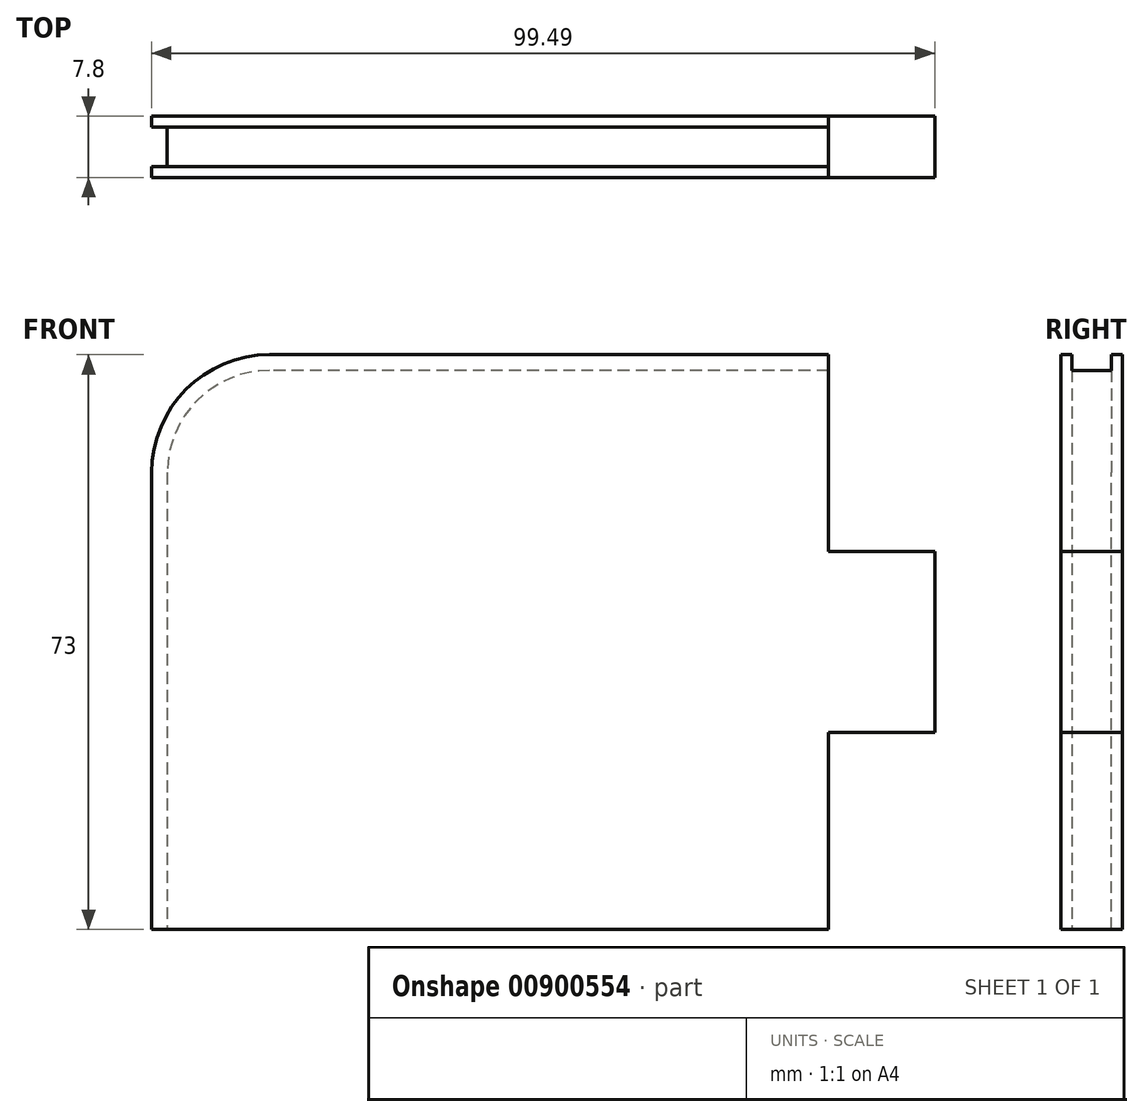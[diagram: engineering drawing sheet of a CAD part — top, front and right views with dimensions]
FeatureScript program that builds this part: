
annotation { "Feature Type Name" : "Feature", "Feature Type Description" : "" }
export const myFeature = defineFeature(function(context is Context, id is Id, definition is map)
    precondition{}
    {
        {
            var Q0;
            Q0=qCreatedBy(makeId("Front.planeOp"),FACE);
            var sketch = newSketch(context, id + "F0", { "sketchPlane" : qUnion([Q0])});
            skLineSegment(sketch, "E0", {"start": v(-28.97, 37.52) * mm, "end": v(42.03, 37.52) * mm});
            skLineSegment(sketch, "E1", {"start": v(42.03, 37.52) * mm, "end": v(42.03, 12.52) * mm});
            skLineSegment(sketch, "E2", {"start": v(42.03, 12.52) * mm, "end": v(55.52, 12.52) * mm});
            skLineSegment(sketch, "E3", {"start": v(55.52, 12.52) * mm, "end": v(55.52, -10.48) * mm});
            skLineSegment(sketch, "E4", {"start": v(55.52, -10.48) * mm, "end": v(42.03, -10.48) * mm});
            skLineSegment(sketch, "E5", {"start": v(42.03, -10.48) * mm, "end": v(42.03, -35.48) * mm});
            skLineSegment(sketch, "E6", {"start": v(42.03, -35.48) * mm, "end": v(-43.97, -35.48) * mm});
            skLineSegment(sketch, "E7", {"start": v(-43.97, -35.48) * mm, "end": v(-43.97, 22.52) * mm});
            skPoint(sketch, "E8.visualSharp", {"position": v(-43.97, 37.52) * mm});
            skArc(sketch, "E8.filletArc", {"start": v(-28.97, 37.52) * mm, "mid": v(-39.58, 33.13) * mm, "end": v(-43.97, 22.52) * mm});
            skSolve(sketch);
        }
        {
            var Q0;
            Q0=makeQuery(id+"F0.imprint","IMPRINT",FACE,{"disambiguationData":[TD([[makeQuery(id+"F0.imprint","IMPRINT",EDGE,{"derivedFrom":sQuery(id+"F0.wireOp",EDGE,"E0")}),-1.0]])]});
            extrude(context, id + "F1", {"entities" : qUnion([Q0]), "oppositeDirection" : true, "depth" : 1.4 * mm, "offsetDistance" : 25 * mm});
        }
        {
            var Q0;
            Q0=makeQuery(id+"F1.opExtrude","CAP_FACE",FACE,{"disambiguationData":[OSD([sQuery(id+"F0.wireOp",EDGE,"E0"),sQuery(id+"F0.wireOp",EDGE,"E1"),sQuery(id+"F0.wireOp",EDGE,"E2"),sQuery(id+"F0.wireOp",EDGE,"E3"),sQuery(id+"F0.wireOp",EDGE,"E4"),sQuery(id+"F0.wireOp",EDGE,"E5"),sQuery(id+"F0.wireOp",EDGE,"E6"),sQuery(id+"F0.wireOp",EDGE,"E7"),sQuery(id+"F0.wireOp",EDGE,"E8.filletArc")])],"isStart":true});
            var sketch = newSketch(context, id + "F2", { "sketchPlane" : qUnion([Q0])});
            skLineSegment(sketch, "E9", {"start": v(42.03, 35.52) * mm, "end": v(-28.97, 35.52) * mm});
            skLineSegment(sketch, "E10", {"start": v(-41.97, 22.52) * mm, "end": v(-41.97, -35.48) * mm});
            skLineSegment(sketch, "E11", {"start": v(-41.97, -35.48) * mm, "end": v(42.03, -35.48) * mm});
            skLineSegment(sketch, "E12", {"start": v(42.03, -35.48) * mm, "end": v(42.03, -10.48) * mm});
            skLineSegment(sketch, "E13", {"start": v(42.03, -10.48) * mm, "end": v(55.52, -10.48) * mm});
            skLineSegment(sketch, "E14", {"start": v(55.52, -10.48) * mm, "end": v(55.52, 12.52) * mm});
            skLineSegment(sketch, "E15", {"start": v(55.52, 12.52) * mm, "end": v(42.03, 12.52) * mm});
            skLineSegment(sketch, "E16", {"start": v(42.03, 12.52) * mm, "end": v(42.03, 35.52) * mm});
            skPoint(sketch, "E17.visualSharp", {"position": v(-41.97, 35.52) * mm});
            skArc(sketch, "E17.filletArc", {"start": v(-28.97, 35.52) * mm, "mid": v(-38.16, 31.72) * mm, "end": v(-41.97, 22.52) * mm});
            skSolve(sketch);
        }
        {
            var Q0;
            Q0 = qSketchRegion(id + "F2", true);
            extrude(context, id + "F3", {"entities" : qUnion([Q0]), "operationType" : NewBodyOperationType.ADD, "depth" : 5 * mm, "offsetDistance" : 25 * mm});
        }
        {
            var Q0;
            Q0=makeQuery(id+"F3.opExtrude","CAP_FACE",FACE,{"disambiguationData":[OSD([sQuery(id+"F2.wireOp",EDGE,"E9"),sQuery(id+"F2.wireOp",EDGE,"E10"),sQuery(id+"F2.wireOp",EDGE,"E11"),sQuery(id+"F2.wireOp",EDGE,"E12"),sQuery(id+"F2.wireOp",EDGE,"E13"),sQuery(id+"F2.wireOp",EDGE,"E14"),sQuery(id+"F2.wireOp",EDGE,"E15"),sQuery(id+"F2.wireOp",EDGE,"E16"),sQuery(id+"F2.wireOp",EDGE,"E17.filletArc")])],"isStart":false});
            var sketch = newSketch(context, id + "F4", { "sketchPlane" : qUnion([Q0])});
            skLineSegment(sketch, "E18", {"start": v(-28.97, 37.52) * mm, "end": v(42.03, 37.52) * mm});
            skLineSegment(sketch, "E19", {"start": v(42.03, 37.52) * mm, "end": v(42.03, 12.52) * mm});
            skLineSegment(sketch, "E20", {"start": v(42.03, 12.52) * mm, "end": v(55.52, 12.52) * mm});
            skLineSegment(sketch, "E21", {"start": v(55.52, 12.52) * mm, "end": v(55.52, -10.48) * mm});
            skLineSegment(sketch, "E22", {"start": v(55.52, -10.48) * mm, "end": v(42.03, -10.48) * mm});
            skLineSegment(sketch, "E23", {"start": v(42.03, -10.48) * mm, "end": v(42.03, -35.48) * mm});
            skLineSegment(sketch, "E24", {"start": v(42.03, -35.48) * mm, "end": v(-43.97, -35.48) * mm});
            skLineSegment(sketch, "E25", {"start": v(-43.97, -35.48) * mm, "end": v(-43.97, 22.52) * mm});
            skPoint(sketch, "E26.visualSharp", {"position": v(-43.97, 37.52) * mm});
            skArc(sketch, "E26.filletArc", {"start": v(-28.97, 37.52) * mm, "mid": v(-39.58, 33.13) * mm, "end": v(-43.97, 22.52) * mm});
            skSolve(sketch);
        }
        {
            var Q0;
            Q0 = qSketchRegion(id + "F4", true);
            extrude(context, id + "F5", {"entities" : qUnion([Q0]), "operationType" : NewBodyOperationType.ADD, "depth" : 1.4 * mm, "offsetDistance" : 25 * mm});
        }
    });
